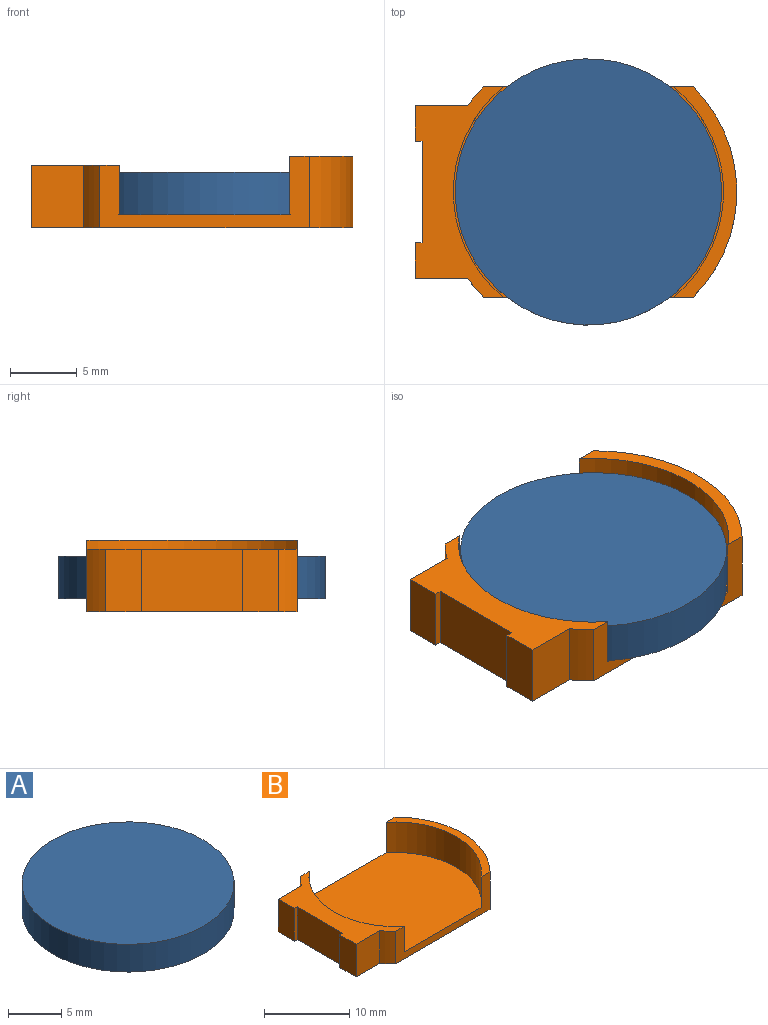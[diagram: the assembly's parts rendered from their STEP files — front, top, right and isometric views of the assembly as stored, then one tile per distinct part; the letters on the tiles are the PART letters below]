
ASSEMBLY  parts=2 mates=1
PART A: 3 faces, bbox 20x20x3.2 mm
  f0: cylinder r=10mm len=20mm, axis (0,0,-1), area 201.1mm2, adj f1,f2
  f1: plane 20x20mm, normal (0,0,1), area 314.2mm2, adj f0
  f2: plane 20x20mm, normal (0,0,-1), area 314.2mm2, adj f0
PART B: 18 faces, bbox 24.2x15.8x5.4 mm
  f0: plane 15.74x5.4mm, normal (0,1,0), area 27.9mm2, adj f10,f11,f12,f13,f14,f15,f16,f17
  f1: plane 4.7x2.7mm, normal (-1,0,0), area 12.7mm2, adj f2,f8,f13,f17
  f2: plane 4.7x0.5mm, normal (0,-1,0), area 2.3mm2, adj f1,f3,f13,f17
  f3: plane 7.6x4.7mm, normal (-1,0,0), area 35.7mm2, adj f2,f4,f13,f17
  f4: plane 4.7x0.5mm, normal (0,1,0), area 2.3mm2, adj f3,f5,f13,f17
  f5: plane 4.7x2.7mm, normal (-1,0,0), area 12.7mm2, adj f4,f6,f13,f17
  f6: plane 4.7x3.94mm, normal (0,-1,0), area 18.5mm2, adj f5,f9,f13,f17
  f7: plane 15.74x5.4mm, normal (0,-1,0), area 27.9mm2, adj f9,f11,f12,f13,f14,f15,f16,f17
  f8: plane 4.7x3.94mm, normal (0,1,0), area 18.5mm2, adj f1,f10,f13,f17
  f9: cylinder r=11.15mm len=4.7mm, axis (0,0,-1), area 8.6mm2, adj f6,f7,f13,f17
  f10: cylinder r=11.15mm len=4.7mm, axis (0,0,-1), area 8.6mm2, adj f0,f8,f13,f17
  f11: cylinder r=11.15mm len=15.8mm, axis (0,0,-1), area 94.8mm2, adj f0,f7,f12,f13
  f12: plane 15.8x4.78mm, normal (0,0,1), area 17.8mm2, adj f0,f7,f11,f15
  f13: plane 24.15x15.8mm, normal (0,0,-1), area 349mm2, adj f0,f1,f2,f3,f4,f5,f6,f7
  f14: cylinder r=10.15mm len=15.8mm, axis (0,0,1), area 67mm2, adj f0,f7,f16,f17
  f15: cylinder r=10.15mm len=15.8mm, axis (0,0,1), area 79.7mm2, adj f0,f7,f12,f16
  f16: plane 20.3x15.8mm, normal (0,0,1), area 284.5mm2, adj f0,f7,f14,f15
  f17: plane 15.8x6.63mm, normal (0,0,1), area 46.8mm2, adj f0,f1,f2,f3,f4,f5,f6,f7
PLACE A t=(0,0,1)mm
PLACE B at identity
MATE fastened A.f0 <-> B.f9  axis (0,0,-1) through (0,0,1)mm
